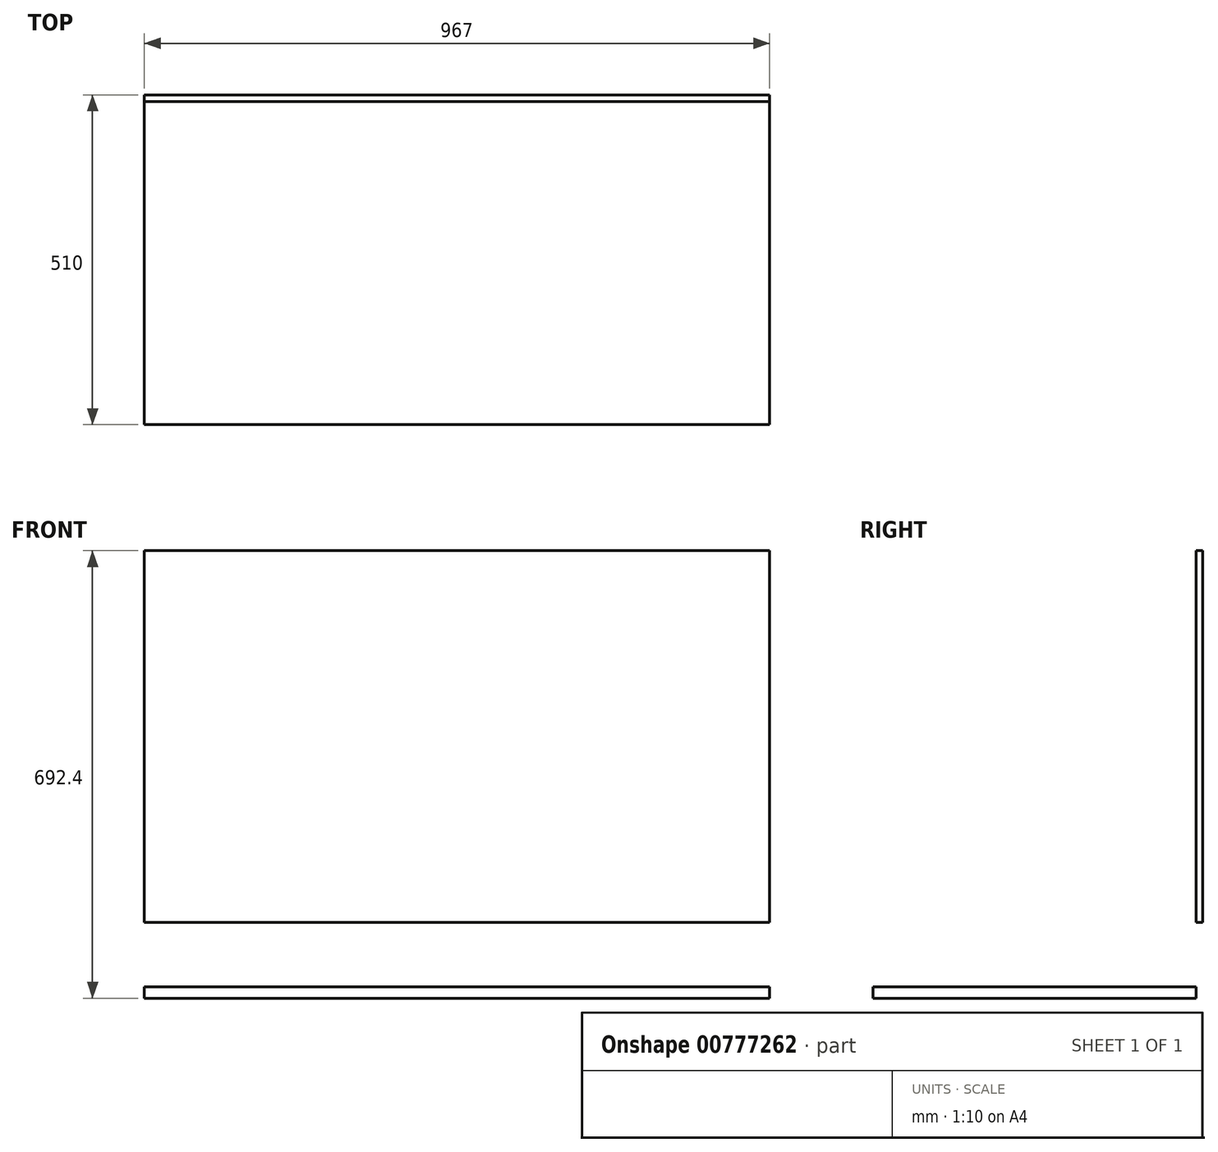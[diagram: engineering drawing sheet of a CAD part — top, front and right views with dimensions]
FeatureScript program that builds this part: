
annotation { "Feature Type Name" : "Feature", "Feature Type Description" : "" }
export const myFeature = defineFeature(function(context is Context, id is Id, definition is map)
    precondition{}
    {
        {
            var Q0;
            Q0=qCreatedBy(makeId("Front.planeOp"),FACE);
            var sketch = newSketch(context, id + "F0", { "sketchPlane" : qUnion([Q0])});
            skLineSegment(sketch, "E0.bottom", {"start": v(0, 0) * mm, "end": v(967, 0) * mm});
            skLineSegment(sketch, "E0.top", {"start": v(0, 575) * mm, "end": v(967, 575) * mm});
            skLineSegment(sketch, "E0.left", {"start": v(0, 0) * mm, "end": v(0, 575) * mm});
            skLineSegment(sketch, "E0.right", {"start": v(967, 0) * mm, "end": v(967, 575) * mm});
            skSolve(sketch);
        }
        {
            var Q0;
            Q0 = qSketchRegion(id + "F0", true);
            extrude(context, id + "F1", {"entities" : qUnion([Q0]), "oppositeDirection" : true, "depth" : 10 * mm, "offsetDistance" : 25 * mm});
        }
        {
            var Q0;
            Q0=qCreatedBy(makeId("Top.planeOp"),FACE);
            cPlane(context, id + "F2", {"entities" : qUnion([Q0]), "cplaneType" : CPlaneType.OFFSET, "offset" : 100 * mm, "oppositeDirection" : true, "width" : 150 * mm, "height" : 150 * mm});
        }
        {
            var Q0;
            Q0=qCreatedBy(id+"F2.planeOp",FACE);
            var sketch = newSketch(context, id + "F3", { "sketchPlane" : qUnion([Q0])});
            skLineSegment(sketch, "E1.bottom", {"start": v(967, 0) * mm, "end": v(0, 0) * mm});
            skLineSegment(sketch, "E1.top", {"start": v(967, -500) * mm, "end": v(0, -500) * mm});
            skLineSegment(sketch, "E1.left", {"start": v(967, 0) * mm, "end": v(967, -500) * mm});
            skLineSegment(sketch, "E1.right", {"start": v(0, 0) * mm, "end": v(0, -500) * mm});
            skSolve(sketch);
        }
        {
            var Q0;
            Q0 = qSketchRegion(id + "F3", true);
            extrude(context, id + "F4", {"entities" : qUnion([Q0]), "oppositeDirection" : true, "depth" : 17.4 * mm, "offsetDistance" : 25 * mm});
        }
    });
